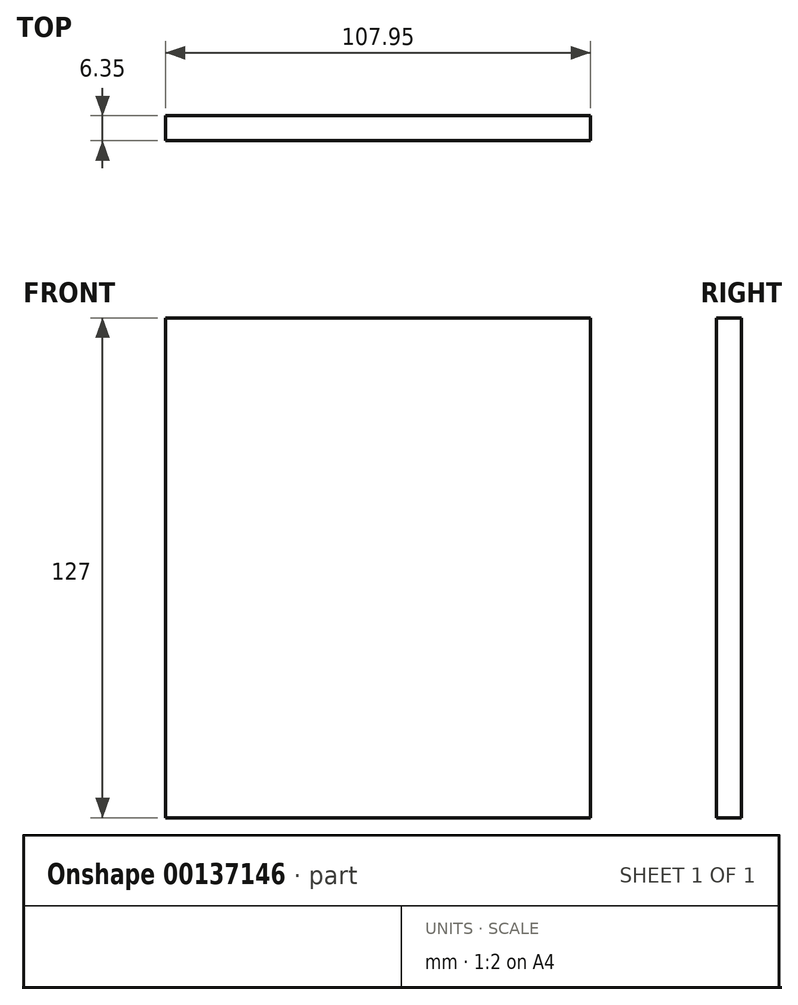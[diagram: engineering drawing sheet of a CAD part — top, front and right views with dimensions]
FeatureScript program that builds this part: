
annotation { "Feature Type Name" : "Feature", "Feature Type Description" : "" }
export const myFeature = defineFeature(function(context is Context, id is Id, definition is map)
    precondition{}
    {
        {
            var Q0;
            Q0=qCreatedBy(makeId("Front.planeOp"),FACE);
            var sketch = newSketch(context, id + "F0", { "sketchPlane" : qUnion([Q0])});
            skLineSegment(sketch, "E0.bottom", {"start": v(0, 0) * mm, "end": v(107.95, 0) * mm});
            skLineSegment(sketch, "E0.top", {"start": v(0, 127) * mm, "end": v(107.95, 127) * mm});
            skLineSegment(sketch, "E0.left", {"start": v(0, 0) * mm, "end": v(0, 127) * mm});
            skLineSegment(sketch, "E0.right", {"start": v(107.95, 0) * mm, "end": v(107.95, 127) * mm});
            skSolve(sketch);
        }
        {
            var Q0;
            Q0=makeQuery(id+"F0.imprint","IMPRINT",FACE,{"disambiguationData":[TD([[makeQuery(id+"F0.imprint","IMPRINT",EDGE,{"derivedFrom":sQuery(id+"F0.wireOp",EDGE,"E0.bottom")}),1.0]])]});
            extrude(context, id + "F1", {"entities" : qUnion([Q0]), "depth" : 6.35 * mm});
        }
    });
